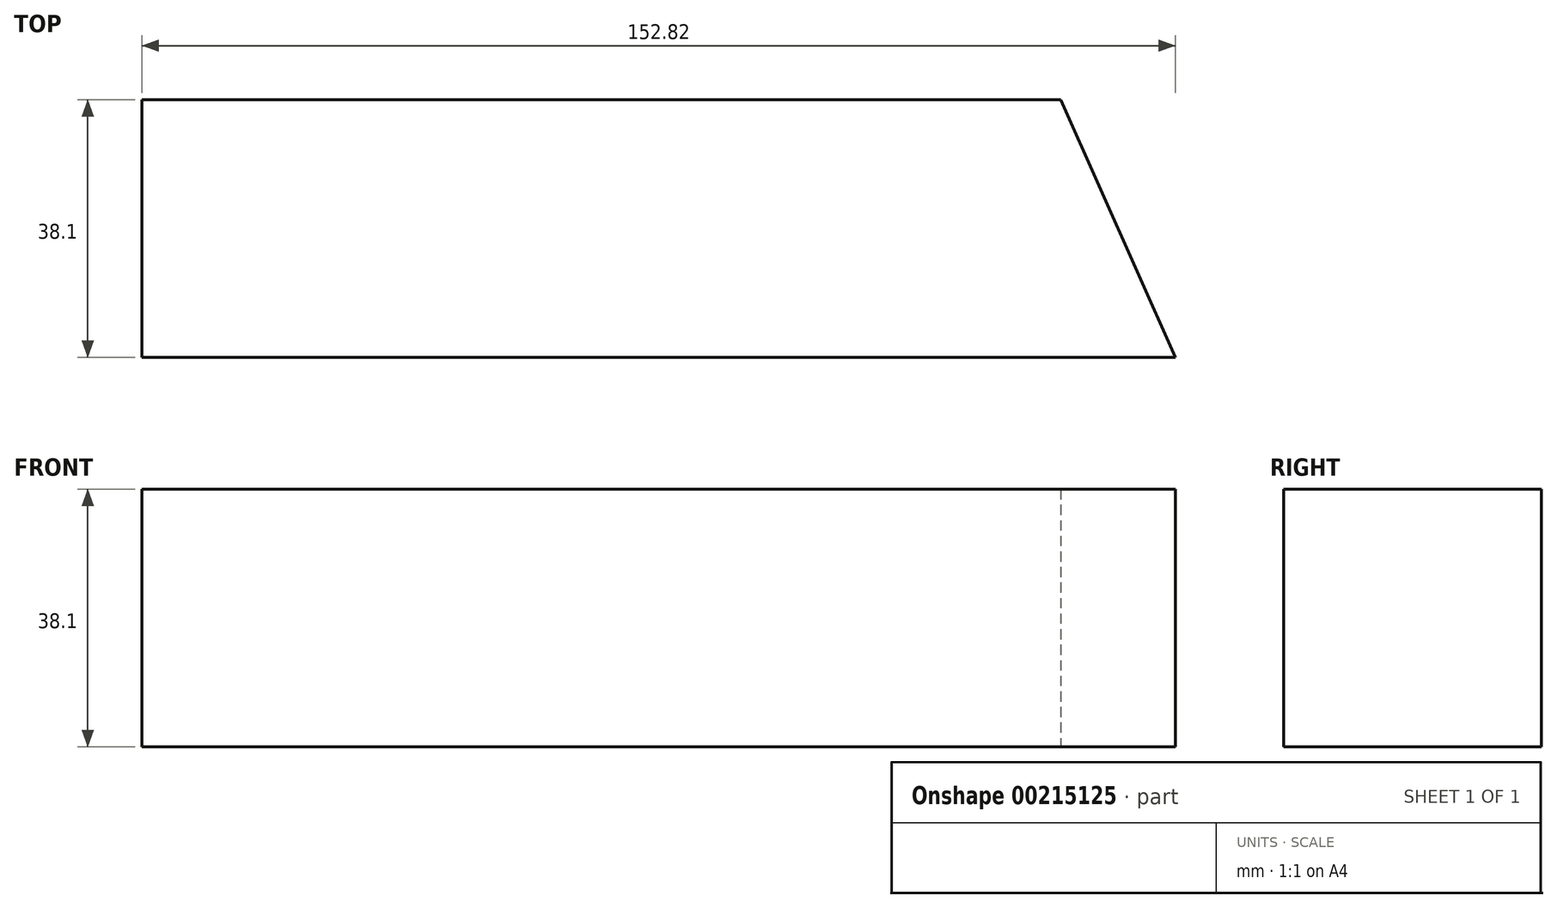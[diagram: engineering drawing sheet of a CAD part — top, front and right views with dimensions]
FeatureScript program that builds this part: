
annotation { "Feature Type Name" : "Feature", "Feature Type Description" : "" }
export const myFeature = defineFeature(function(context is Context, id is Id, definition is map)
    precondition{}
    {
        {
            var Q0;
            Q0=qCreatedBy(makeId("Top.planeOp"),FACE);
            var sketch = newSketch(context, id + "F0", { "sketchPlane" : qUnion([Q0])});
            skLineSegment(sketch, "E0", {"start": v(0, 0) * mm, "end": v(152.82, 0) * mm});
            skLineSegment(sketch, "E1", {"start": v(152.82, 0) * mm, "end": v(135.86, 38.1) * mm});
            skLineSegment(sketch, "E2", {"start": v(135.86, 38.1) * mm, "end": v(0, 38.1) * mm});
            skLineSegment(sketch, "E3", {"start": v(0, 38.1) * mm, "end": v(0, 0) * mm});
            skSolve(sketch);
        }
        {
            var Q0;
            Q0=makeQuery(id+"F0.imprint","IMPRINT",FACE,{"disambiguationData":[TD([[makeQuery(id+"F0.imprint","IMPRINT",EDGE,{"derivedFrom":sQuery(id+"F0.wireOp",EDGE,"E0")}),1.0]])]});
            extrude(context, id + "F1", {"entities" : qUnion([Q0]), "depth" : 38.1 * mm, "offsetDistance" : 25.4 * mm});
        }
    });
